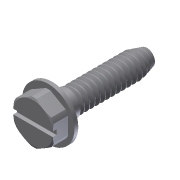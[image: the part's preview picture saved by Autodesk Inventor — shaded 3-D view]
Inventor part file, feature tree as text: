
AUTODESK INVENTOR PART (.ipt)
format: ipt  version: 2011 (Build 150239000, 239)  size: 545,280 bytes
history: native  units: in
note: dims shown in document units (in); Inventor stores cm internally (conversion verified against a paired STEP export)
features: other x1, imported_body x1, extrude x1, sketch x1
ambient origin geometry x8: Origin, YZ Plane, XZ Plane, XY Plane, X Axis, Y Axis, Z Axis, Center Point
feature tree (4):
  parser-record x1  (decoder bookkeeping rows leaked as tree rows — omitted from the tree; the rows remain in map.json)
  imported_body  "Base1"
  extrude  "Extrusion1"  Depth=0.125in TaperAngle=0.0deg
  sketch  "Sketch1"  dims[d0=0.2in d1=0.125in d2=0.0in]
